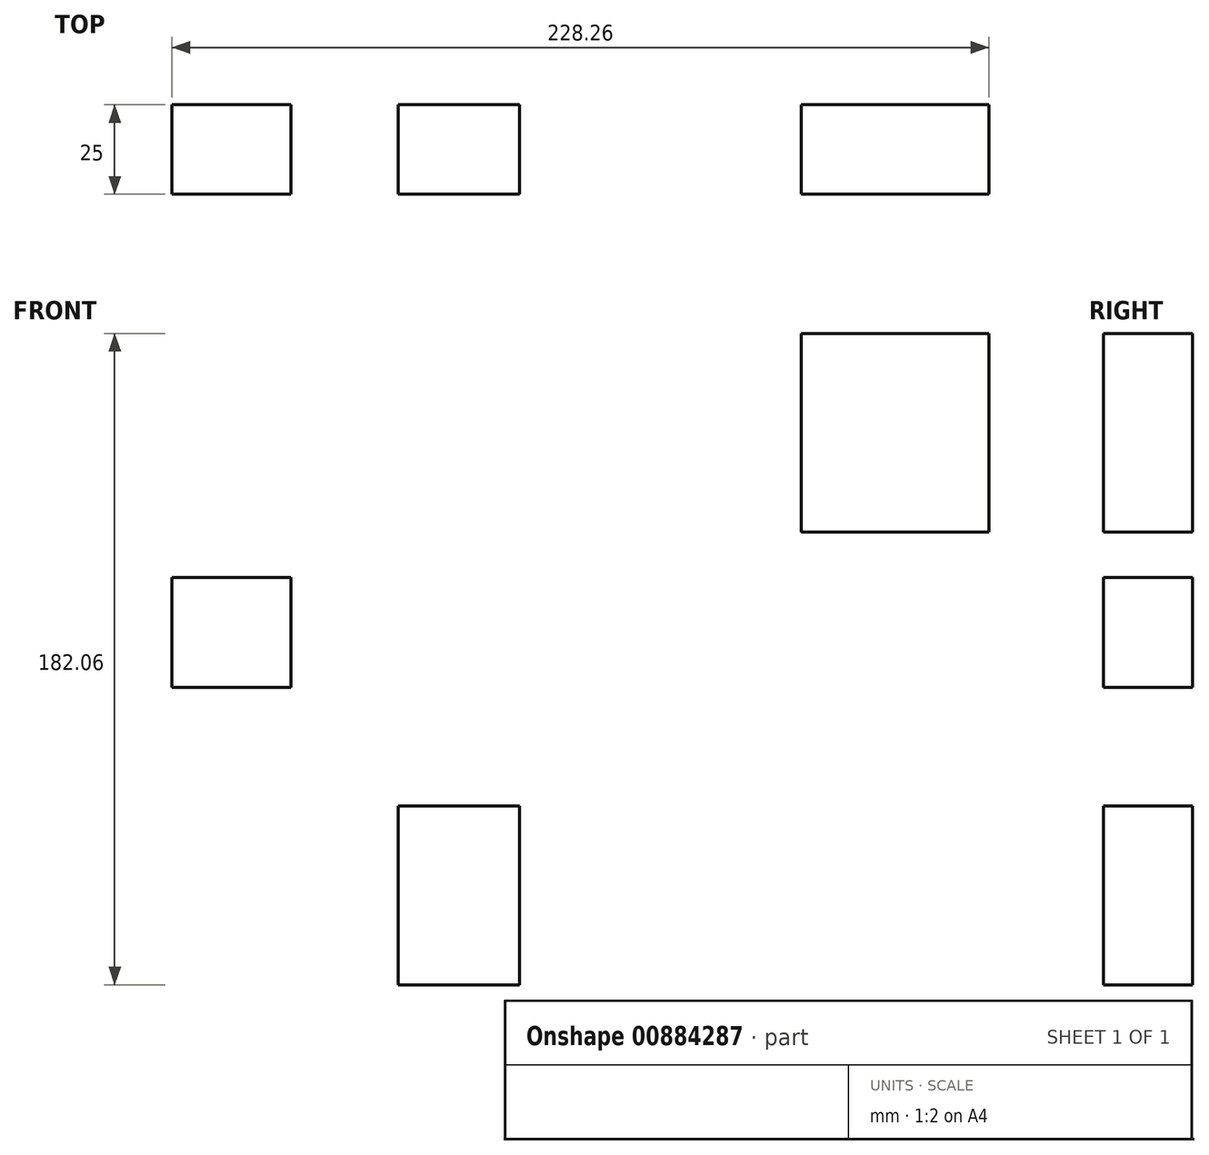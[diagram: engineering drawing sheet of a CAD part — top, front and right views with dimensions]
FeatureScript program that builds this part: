
annotation { "Feature Type Name" : "Feature", "Feature Type Description" : "" }
export const myFeature = defineFeature(function(context is Context, id is Id, definition is map)
    precondition{}
    {
        {
            var Q0;
            Q0=qCreatedBy(makeId("Front.planeOp"),FACE);
            var sketch = newSketch(context, id + "F0", { "sketchPlane" : qUnion([Q0])});
            skLineSegment(sketch, "E0.bottom", {"start": v(-125.56, 16.37) * mm, "end": v(-92.28, 16.37) * mm});
            skLineSegment(sketch, "E0.top", {"start": v(-125.56, -14.37) * mm, "end": v(-92.28, -14.37) * mm});
            skLineSegment(sketch, "E0.left", {"start": v(-125.56, 16.37) * mm, "end": v(-125.56, -14.37) * mm});
            skLineSegment(sketch, "E0.right", {"start": v(-92.28, 16.37) * mm, "end": v(-92.28, -14.37) * mm});
            skLineSegment(sketch, "E1.bottom", {"start": v(-62.36, -47.42) * mm, "end": v(-28.4, -47.42) * mm});
            skLineSegment(sketch, "E1.top", {"start": v(-62.36, -97.46) * mm, "end": v(-28.4, -97.46) * mm});
            skLineSegment(sketch, "E1.left", {"start": v(-62.36, -47.42) * mm, "end": v(-62.36, -97.46) * mm});
            skLineSegment(sketch, "E1.right", {"start": v(-28.4, -47.42) * mm, "end": v(-28.4, -97.46) * mm});
            skLineSegment(sketch, "E2.bottom", {"start": v(50.26, 84.6) * mm, "end": v(102.7, 84.6) * mm});
            skLineSegment(sketch, "E2.top", {"start": v(50.26, 29.14) * mm, "end": v(102.7, 29.14) * mm});
            skLineSegment(sketch, "E2.left", {"start": v(50.26, 84.6) * mm, "end": v(50.26, 29.14) * mm});
            skLineSegment(sketch, "E2.right", {"start": v(102.7, 84.6) * mm, "end": v(102.7, 29.14) * mm});
            skSolve(sketch);
        }
        {
            var Q0;
            Q0=makeQuery(id+"F0.imprint","IMPRINT",FACE,{"disambiguationData":[TD([[makeQuery(id+"F0.imprint","IMPRINT",EDGE,{"derivedFrom":sQuery(id+"F0.wireOp",EDGE,"E0.bottom")}),-1.0]])]});
            extrude(context, id + "F1", {"entities" : qUnion([Q0]), "depth" : 25 * mm, "offsetDistance" : 25 * mm});
        }
        {
            var Q0;
            Q0=makeQuery(id+"F0.imprint","IMPRINT",FACE,{"disambiguationData":[TD([[makeQuery(id+"F0.imprint","IMPRINT",EDGE,{"derivedFrom":sQuery(id+"F0.wireOp",EDGE,"E1.bottom")}),-1.0]])]});
            extrude(context, id + "F2", {"entities" : qUnion([Q0]), "depth" : 25 * mm, "offsetDistance" : 25 * mm});
        }
        {
            var Q0;
            Q0=makeQuery(id+"F0.imprint","IMPRINT",FACE,{"disambiguationData":[TD([[makeQuery(id+"F0.imprint","IMPRINT",EDGE,{"derivedFrom":sQuery(id+"F0.wireOp",EDGE,"E2.bottom")}),-1.0]])]});
            extrude(context, id + "F3", {"entities" : qUnion([Q0]), "depth" : 25 * mm, "offsetDistance" : 25 * mm});
        }
    });
